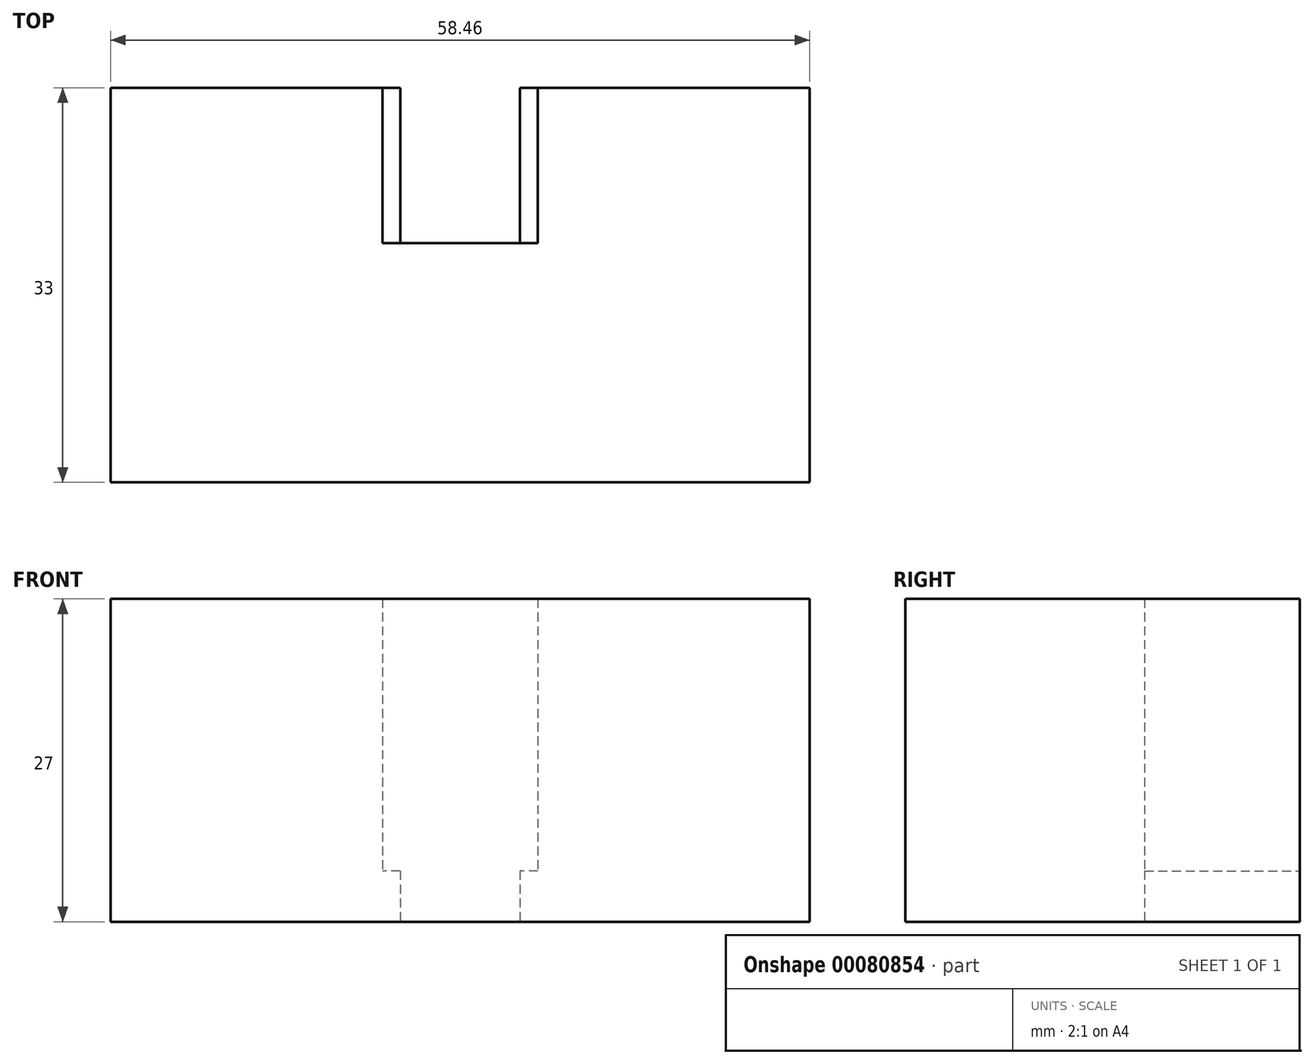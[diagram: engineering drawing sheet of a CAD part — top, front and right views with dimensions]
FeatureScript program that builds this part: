
annotation { "Feature Type Name" : "Feature", "Feature Type Description" : "" }
export const myFeature = defineFeature(function(context is Context, id is Id, definition is map)
    precondition{}
    {
        {
            var Q0;
            Q0=qCreatedBy(makeId("Top.planeOp"),FACE);
            var sketch = newSketch(context, id + "F0", { "sketchPlane" : qUnion([Q0])});
            skLineSegment(sketch, "E0.bottom", {"start": v(29.22, 16.5) * mm, "end": v(-29.23, 16.5) * mm});
            skLineSegment(sketch, "E0.top", {"start": v(29.22, -16.5) * mm, "end": v(-29.22, -16.5) * mm});
            skLineSegment(sketch, "E0.left", {"start": v(29.22, 16.5) * mm, "end": v(29.23, -16.5) * mm});
            skLineSegment(sketch, "E0.right", {"start": v(-29.23, 16.5) * mm, "end": v(-29.22, -16.5) * mm});
            skPoint(sketch, "E0.middle", {"position": v(0, 0) * mm});
            skLineSegment(sketch, "E1", {"start": v(-10.25, 16.5) * mm, "end": v(-10.25, -16.5) * mm});
            skLineSegment(sketch, "E2", {"start": v(10.25, 16.5) * mm, "end": v(10.25, -16.5) * mm});
            skSolve(sketch);
        }
        {
            var Q0;
            Q0 = qSketchRegion(id + "F0", true);
            extrude(context, id + "F1", {"entities" : qUnion([Q0]), "depth" : 27 * mm});
        }
        {
            var Q0;
            {var subQ0=sQuery(id+"F0.wireOp",EDGE,"E0.right");Q0=makeQuery(id+"F0.imprint","IMPRINT",FACE,{"disambiguationData":[TD([[makeQuery(id+"F0.imprint","IMPRINT",EDGE,{"derivedFrom":subQ0}),1.0]])]});}
            var sketch = newSketch(context, id + "F2", { "sketchPlane" : qUnion([Q0])});
            skLineSegment(sketch, "E3.bottom", {"start": v(-6.5, 3.5) * mm, "end": v(6.5, 3.5) * mm});
            skLineSegment(sketch, "E3.top", {"start": v(-6.5, 16.5) * mm, "end": v(6.5, 16.5) * mm});
            skLineSegment(sketch, "E3.left", {"start": v(-6.5, 3.5) * mm, "end": v(-6.5, 16.5) * mm});
            skLineSegment(sketch, "E3.right", {"start": v(6.5, 3.5) * mm, "end": v(6.5, 16.5) * mm});
            skSolve(sketch);
        }
        {
            var Q0;
            Q0 = qSketchRegion(id + "F2", true);
            extrude(context, id + "F3", {"entities" : qUnion([Q0]), "operationType" : NewBodyOperationType.REMOVE, "endBound" : BoundingType.THROUGH_ALL, "depth" : 25 * mm});
        }
        {
            var Q0;
            {var subQ0=sQuery(id+"F0.wireOp",EDGE,"E1");Q0=makeQuery(id+"F0.imprint","IMPRINT",FACE,{"disambiguationData":[TD([[makeQuery(id+"F0.imprint","IMPRINT",EDGE,{"derivedFrom":subQ0}),1.0]])]});}
            var sketch = newSketch(context, id + "F4", { "sketchPlane" : qUnion([Q0])});
            skLineSegment(sketch, "E4.bottom", {"start": v(-6.5, 3.5) * mm, "end": v(-5, 3.5) * mm});
            skLineSegment(sketch, "E4.top", {"start": v(-6.5, 16.5) * mm, "end": v(-5, 16.5) * mm});
            skLineSegment(sketch, "E4.left", {"start": v(-6.5, 3.5) * mm, "end": v(-6.5, 16.5) * mm});
            skLineSegment(sketch, "E4.right", {"start": v(-5, 3.5) * mm, "end": v(-5, 16.5) * mm});
            skLineSegment(sketch, "E5.bottom", {"start": v(5, 3.5) * mm, "end": v(6.5, 3.5) * mm});
            skLineSegment(sketch, "E5.top", {"start": v(5, 16.5) * mm, "end": v(6.5, 16.5) * mm});
            skLineSegment(sketch, "E5.left", {"start": v(5, 3.5) * mm, "end": v(5, 16.5) * mm});
            skLineSegment(sketch, "E5.right", {"start": v(6.5, 3.5) * mm, "end": v(6.5, 16.5) * mm});
            skSolve(sketch);
        }
        {
            var Q0;
            Q0 = qSketchRegion(id + "F4", true);
            extrude(context, id + "F5", {"entities" : qUnion([Q0]), "operationType" : NewBodyOperationType.ADD, "depth" : 4.25 * mm});
        }
    });
